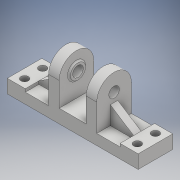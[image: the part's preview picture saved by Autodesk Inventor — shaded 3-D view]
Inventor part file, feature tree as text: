
AUTODESK INVENTOR PART (.ipt)
format: ipt  version: 2018 (Build 220112000, 112)  size: 218,624 bytes
history: native  units: mm
features: sketch x5, extrude x3, revolve x1, fillet x1, rib x1, mirror x1, projected_geometry x1, plane x1
ambient origin geometry x8: Origin, YZ Plane, XZ Plane, XY Plane, X Axis, Y Axis, Z Axis, Center Point
bodies: Solid1 (feature_tree)
feature tree (14):
  extrude  "Extrusion1"  Depth=46.0mm
  extrude  "Extrusion2"  Depth=24.0mm
  revolve  "Revolution1"  [1 undecoded]
  extrude  "Extrusion3"  Depth=24.0mm
  fillet  "Fillet1"  Radius=55.0mm
  rib  "Rib1"
  mirror  "Mirror1"
  sketch  "Sketch1"  dims[d0=174.0mm d1=46.0mm]
  sketch  "Sketch2"  dims[d3=10.0mm d4=20.0mm d6=24.0mm d7=20.0mm d9=150.0mm]
  sketch  "Sketch3"  dims[d12=11.0mm d13=12.0mm]
  sketch  "Sketch4"  dims[d14=18.0mm d15=0.0mm d16=24.0mm d17=55.0mm]
  sketch  "Sketch8"  dims[d18=46.0mm d19=4.0mm d20=0.0mm d21=50.0mm d22=14.0mm d23=46.0mm d24=16.0mm d25=14.0mm d26=3.0mm d27=90.0deg d28=14.0mm d29=4.0mm d30=0.0mm d31=2.0mm d35=12.0mm d37=3.0mm d38=10.0mm d39=0.0mm d40=0.0mm d41=1.0mm d42=1.0mm]
  projected_geometry  "Projected Loop1"
  plane  "Work Plane2"
note: 1 required parameter value undecoded (feature->parameter linkage not recoverable at this tier; creation-order binding heuristic only, values carry confidence <= 0.55)
